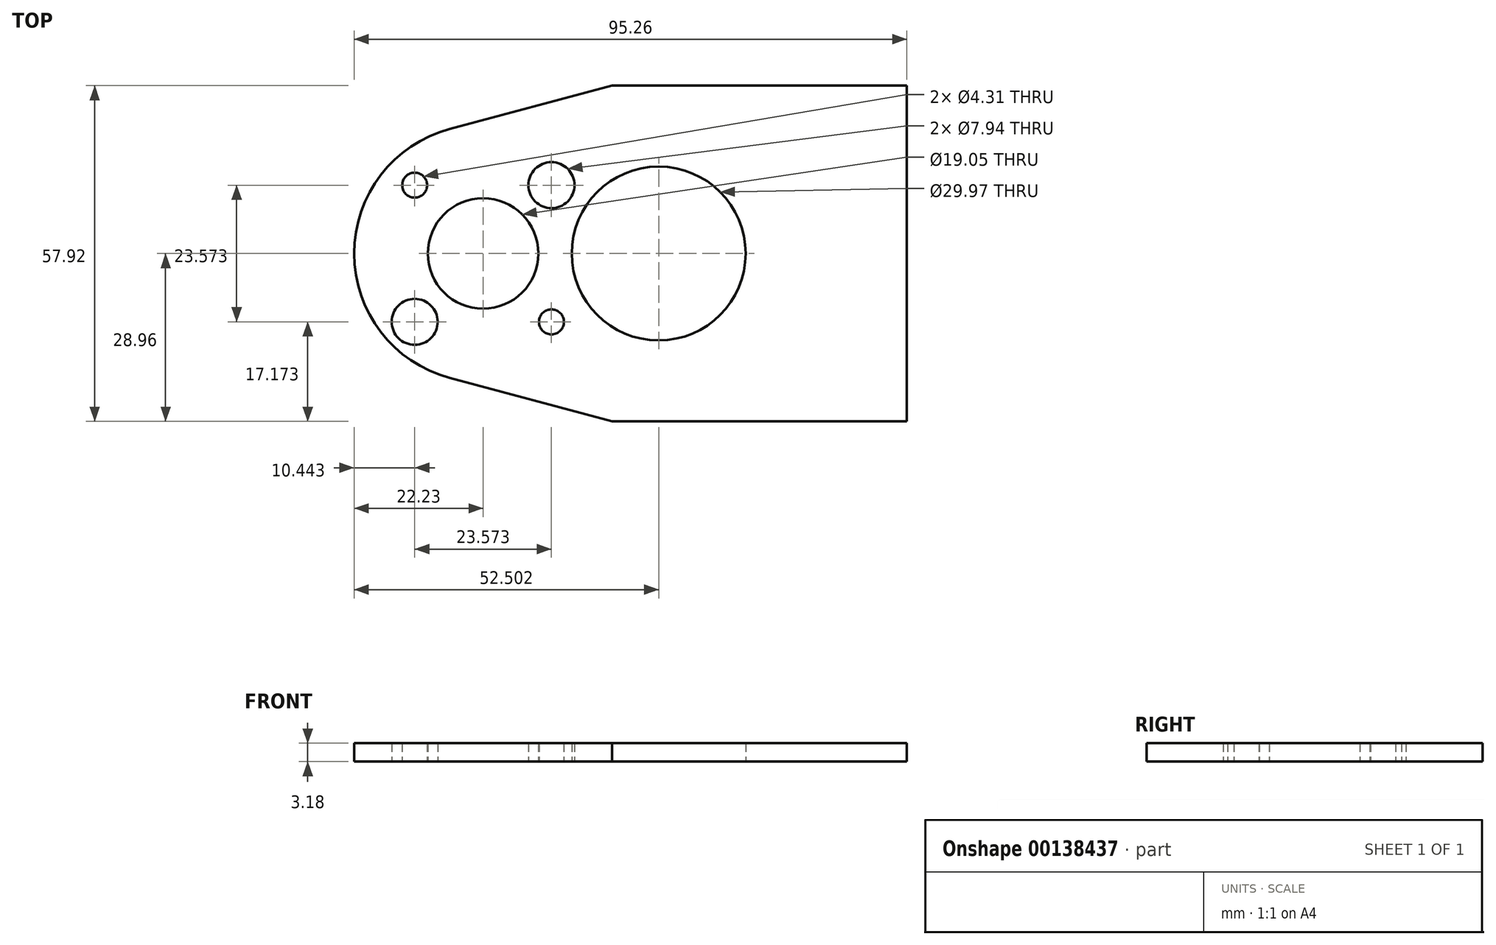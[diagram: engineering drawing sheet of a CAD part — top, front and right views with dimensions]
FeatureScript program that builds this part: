
annotation { "Feature Type Name" : "Feature", "Feature Type Description" : "" }
export const myFeature = defineFeature(function(context is Context, id is Id, definition is map)
    precondition{}
    {
        {
            var Q0;
            Q0=qCreatedBy(makeId("Top.planeOp"),FACE);
            var sketch = newSketch(context, id + "F0", { "sketchPlane" : qUnion([Q0])});
            skCircle(sketch, "E0", {"center": v(0, 0) * mm, "radius": 9.53 * mm});
            skLineSegment(sketch, "E1.bottom", {"start": v(-11.79, 11.79) * mm, "end": v(11.79, 11.79) * mm, "construction": true});
            skLineSegment(sketch, "E1.top", {"start": v(-11.79, -11.79) * mm, "end": v(11.79, -11.79) * mm, "construction": true});
            skLineSegment(sketch, "E1.left", {"start": v(-11.79, 11.79) * mm, "end": v(-11.79, -11.79) * mm, "construction": true});
            skLineSegment(sketch, "E1.right", {"start": v(11.79, 11.79) * mm, "end": v(11.79, -11.79) * mm, "construction": true});
            skCircle(sketch, "E2", {"center": v(0, 0) * mm, "radius": 11.11 * mm, "construction": true});
            skCircle(sketch, "E3", {"center": v(-11.79, 11.79) * mm, "radius": 5.56 * mm, "construction": true});
            skCircle(sketch, "E4", {"center": v(-11.79, 11.79) * mm, "radius": 2.15 * mm});
            skCircle(sketch, "E5", {"center": v(11.79, 11.79) * mm, "radius": 3.97 * mm});
            skCircle(sketch, "E6", {"center": v(-11.79, -11.79) * mm, "radius": 3.97 * mm});
            skCircle(sketch, "E7", {"center": v(11.79, -11.79) * mm, "radius": 2.15 * mm});
            skLineSegment(sketch, "E8", {"start": v(0, 0) * mm, "end": v(22.23, 0) * mm, "construction": true});
            skLineSegment(sketch, "E9.bottom", {"start": v(22.23, 28.96) * mm, "end": v(73.03, 28.96) * mm});
            skLineSegment(sketch, "E9.top", {"start": v(22.23, -28.96) * mm, "end": v(73.03, -28.96) * mm});
            skLineSegment(sketch, "E9.left", {"start": v(22.23, 28.96) * mm, "end": v(22.23, -28.96) * mm, "construction": true});
            skLineSegment(sketch, "E9.right", {"start": v(73.03, 28.96) * mm, "end": v(73.03, -28.96) * mm});
            skArc(sketch, "E10", {"start": v(-5.75, 21.47) * mm, "mid": v(-22.22, 0) * mm, "end": v(-5.75, -21.47) * mm});
            skLineSegment(sketch, "E11", {"start": v(-5.75, 21.47) * mm, "end": v(22.23, 28.96) * mm});
            skLineSegment(sketch, "E12", {"start": v(-5.75, -21.47) * mm, "end": v(22.23, -28.96) * mm});
            skLineSegment(sketch, "E13", {"start": v(-5.75, 21.47) * mm, "end": v(8.24, 21.47) * mm, "construction": true});
            skLineSegment(sketch, "E14", {"start": v(8.24, 21.47) * mm, "end": v(8.24, 25.22) * mm, "construction": true});
            skLineSegment(sketch, "E15", {"start": v(22.23, 0) * mm, "end": v(30.27, 0) * mm, "construction": true});
            skCircle(sketch, "E16", {"center": v(30.27, 0) * mm, "radius": 14.99 * mm});
            skSolve(sketch);
        }
        {
            var Q0;
            Q0=qSketchRegion(id+"F0",true);
            extrude(context, id + "F1", {"entities" : qUnion([Q0]), "depth" : 3.17 * mm});
        }
    });
